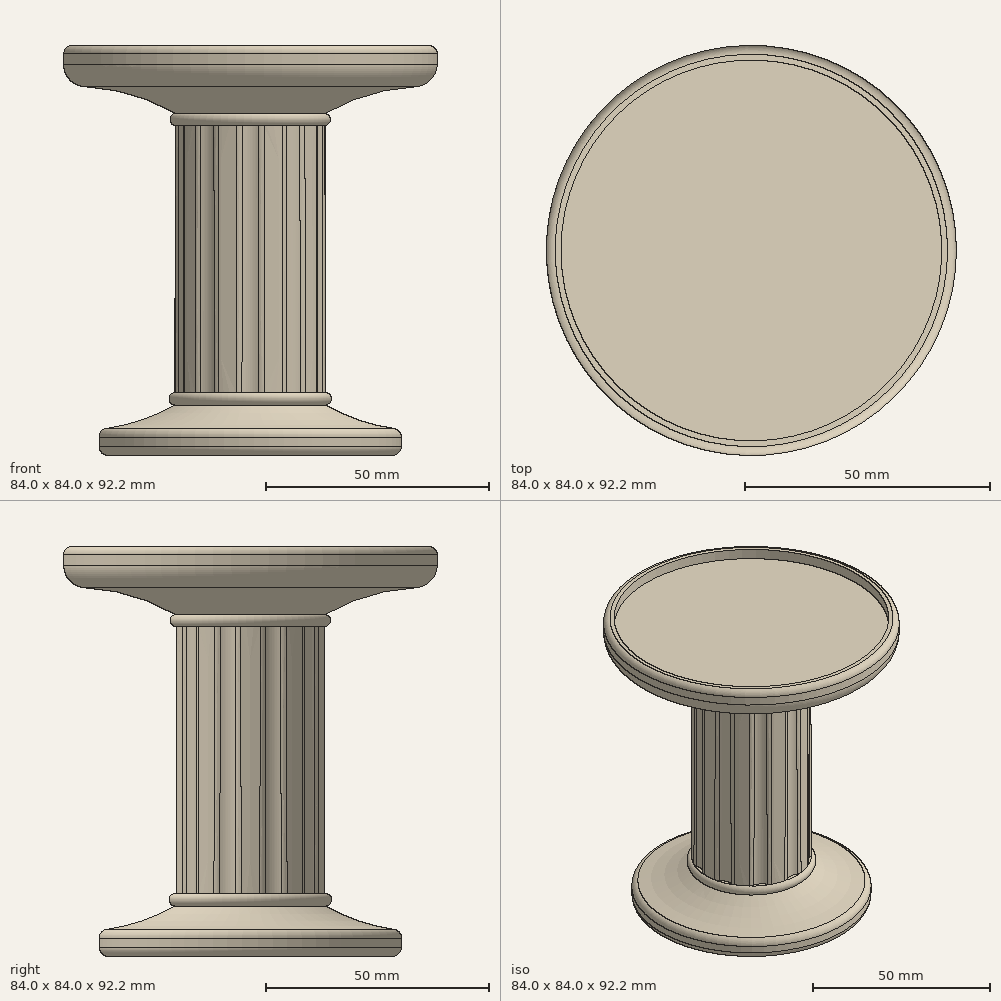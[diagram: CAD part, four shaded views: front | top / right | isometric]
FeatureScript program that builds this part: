
annotation { "Feature Type Name" : "Feature", "Feature Type Description" : "" }
export const myFeature = defineFeature(function(context is Context, id is Id, definition is map)
    precondition{}
    {
        {
            var Q0;
            Q0=qCreatedBy(makeId("Front.planeOp"),FACE);
            var sketch = newSketch(context, id + "F0", { "sketchPlane" : qUnion([Q0])});
            skLineSegment(sketch, "E0", {"start": v(-42, 62.68) * mm, "end": v(-42, 68.97) * mm});
            skLineSegment(sketch, "E1", {"start": v(-39, 68.97) * mm, "end": v(0, 68.97) * mm});
            skLineSegment(sketch, "E2", {"start": v(-34, -16.13) * mm, "end": v(-34, -18.24) * mm});
            skLineSegment(sketch, "E3", {"start": v(-32, -20.24) * mm, "end": v(0, -20.24) * mm});
            skLineSegment(sketch, "E4.0", {"start": v(-17, -6.1) * mm, "end": v(-16.89, 53.9) * mm});
            skArc(sketch, "E5", {"start": v(-16.88, 56.66) * mm, "mid": v(-29, 61.51) * mm, "end": v(-42, 62.68) * mm});
            skArc(sketch, "E6", {"start": v(-16.88, 56.66) * mm, "mid": v(-18.04, 55.29) * mm, "end": v(-16.89, 53.9) * mm});
            skArc(sketch, "E7.MirrorCS", {"start": v(-17, -8.88) * mm, "mid": v(-18.29, -7.49) * mm, "end": v(-17, -6.1) * mm});
            skArc(sketch, "E8.MirrorCS", {"start": v(-17, -8.88) * mm, "mid": v(-24.38, -12.26) * mm, "end": v(-32.27, -14.15) * mm});
            skLineSegment(sketch, "E9", {"start": v(-42, 68.97) * mm, "end": v(-42, 71.97) * mm});
            skLineSegment(sketch, "E10", {"start": v(-42, 71.97) * mm, "end": v(-39, 71.97) * mm});
            skLineSegment(sketch, "E11", {"start": v(-39, 71.97) * mm, "end": v(-39, 68.97) * mm});
            skPoint(sketch, "E12.visualSharp", {"position": v(-34, -20.24) * mm});
            skArc(sketch, "E12.filletArc", {"start": v(-34, -18.24) * mm, "mid": v(-33.41, -19.65) * mm, "end": v(-32, -20.24) * mm});
            skPoint(sketch, "E13.visualSharp", {"position": v(-34, -14.35) * mm});
            skArc(sketch, "E13.filletArc", {"start": v(-32.27, -14.15) * mm, "mid": v(-33.5, -14.81) * mm, "end": v(-34, -16.13) * mm});
            skLineSegment(sketch, "E14", {"start": v(0, -20.24) * mm, "end": v(0, 68.97) * mm});
            skSolve(sketch);
        }
        {
            var Q0;
            Q0=makeQuery(id+"F0.imprint","IMPRINT",FACE,{"disambiguationData":[TD([[makeQuery(id+"F0.imprint","IMPRINT",EDGE,{"derivedFrom":sQuery(id+"F0.wireOp",EDGE,"E0")}),-1.0]])]});
            var Q1;
            Q1=sQuery(id+"F0.wireOp",EDGE,"E14");
            revolve(context, id + "F1", {"entities" : qUnion([Q0]), "axis" : qUnion([Q1]), "revolveType" : RevolveType.FULL});
        }
        {
            var Q0;
            Q0=qCreatedBy(makeId("Top.planeOp"),FACE);
            cPlane(context, id + "F2", {"entities" : qUnion([Q0]), "cplaneType" : CPlaneType.OFFSET, "offset" : 6.1 * mm, "oppositeDirection" : true, "width" : 150 * mm, "height" : 150 * mm});
        }
        {
            var Q0;
            Q0=qCreatedBy(id+"F2.planeOp",FACE);
            var sketch = newSketch(context, id + "F3", { "sketchPlane" : qUnion([Q0])});
            skCircle(sketch, "E15", {"center": v(0, -20) * mm, "radius": 4 * mm});
            skCircle(sketch, "E16.1.0", {"center": v(11.76, -16.18) * mm, "radius": 4 * mm});
            skCircle(sketch, "E16.2.0", {"center": v(19.02, -6.18) * mm, "radius": 4 * mm});
            skCircle(sketch, "E16.3.0", {"center": v(19.02, 6.18) * mm, "radius": 4 * mm});
            skCircle(sketch, "E16.4.0", {"center": v(11.76, 16.18) * mm, "radius": 4 * mm});
            skCircle(sketch, "E16.5.0", {"center": v(0, 20) * mm, "radius": 4 * mm});
            skCircle(sketch, "E16.6.0", {"center": v(-11.76, 16.18) * mm, "radius": 4 * mm});
            skCircle(sketch, "E16.7.0", {"center": v(-19.02, 6.18) * mm, "radius": 4 * mm});
            skCircle(sketch, "E16.8.0", {"center": v(-19.02, -6.18) * mm, "radius": 4 * mm});
            skCircle(sketch, "E16.9.0", {"center": v(-11.76, -16.18) * mm, "radius": 4 * mm});
            skPoint(sketch, "E16.center", {"position": v(0, 0) * mm});
            skSolve(sketch);
        }
        {
            var Q0;
            Q0 = qSketchRegion(id + "F3", true);
            extrude(context, id + "F4", {"entities" : qUnion([Q0]), "operationType" : NewBodyOperationType.REMOVE, "depth" : 60 * mm});
        }
        {
            var Q0;
            Q0=makeQuery(id+"F4.boolean.opBoolean","INTERSECT",EDGE,{"disambiguationData":[OD(1.0)],"derivedFrom":[makeQuery(id+"F1.opRevolve","SWEPT_FACE",FACE,{"disambiguationData":[OSD([sQuery(id+"F0.wireOp",EDGE,"E4.0")])]}),makeQuery(id+"F4.opExtrude","SWEPT_FACE",FACE,{"disambiguationData":[OSD([sQuery(id+"F3.wireOp",EDGE,"E16.9.0")])]})]});
            var Q1;
            Q1=makeQuery(id+"F4.boolean.opBoolean","INTERSECT",EDGE,{"disambiguationData":[OD(0.0)],"derivedFrom":[makeQuery(id+"F1.opRevolve","SWEPT_FACE",FACE,{"disambiguationData":[OSD([sQuery(id+"F0.wireOp",EDGE,"E4.0")])]}),makeQuery(id+"F4.opExtrude","SWEPT_FACE",FACE,{"disambiguationData":[OSD([sQuery(id+"F3.wireOp",EDGE,"E15")])]})]});
            var Q2;
            Q2=makeQuery(id+"F4.boolean.opBoolean","INTERSECT",EDGE,{"disambiguationData":[OD(1.0)],"derivedFrom":[makeQuery(id+"F1.opRevolve","SWEPT_FACE",FACE,{"disambiguationData":[OSD([sQuery(id+"F0.wireOp",EDGE,"E4.0")])]}),makeQuery(id+"F4.opExtrude","SWEPT_FACE",FACE,{"disambiguationData":[OSD([sQuery(id+"F3.wireOp",EDGE,"E15")])]})]});
            var Q3;
            Q3=makeQuery(id+"F4.boolean.opBoolean","INTERSECT",EDGE,{"disambiguationData":[OD(0.0)],"derivedFrom":[makeQuery(id+"F1.opRevolve","SWEPT_FACE",FACE,{"disambiguationData":[OSD([sQuery(id+"F0.wireOp",EDGE,"E4.0")])]}),makeQuery(id+"F4.opExtrude","SWEPT_FACE",FACE,{"disambiguationData":[OSD([sQuery(id+"F3.wireOp",EDGE,"E16.9.0")])]})]});
            var Q4;
            Q4=makeQuery(id+"F4.boolean.opBoolean","INTERSECT",EDGE,{"disambiguationData":[OD(0.0)],"derivedFrom":[makeQuery(id+"F1.opRevolve","SWEPT_FACE",FACE,{"disambiguationData":[OSD([sQuery(id+"F0.wireOp",EDGE,"E4.0")])]}),makeQuery(id+"F4.opExtrude","SWEPT_FACE",FACE,{"disambiguationData":[OSD([sQuery(id+"F3.wireOp",EDGE,"E16.8.0")])]})]});
            var Q5;
            Q5=makeQuery(id+"F4.boolean.opBoolean","INTERSECT",EDGE,{"disambiguationData":[OD(1.0)],"derivedFrom":[makeQuery(id+"F1.opRevolve","SWEPT_FACE",FACE,{"disambiguationData":[OSD([sQuery(id+"F0.wireOp",EDGE,"E4.0")])]}),makeQuery(id+"F4.opExtrude","SWEPT_FACE",FACE,{"disambiguationData":[OSD([sQuery(id+"F3.wireOp",EDGE,"E16.8.0")])]})]});
            var Q6;
            Q6=makeQuery(id+"F4.boolean.opBoolean","INTERSECT",EDGE,{"disambiguationData":[OD(0.0)],"derivedFrom":[makeQuery(id+"F1.opRevolve","SWEPT_FACE",FACE,{"disambiguationData":[OSD([sQuery(id+"F0.wireOp",EDGE,"E4.0")])]}),makeQuery(id+"F4.opExtrude","SWEPT_FACE",FACE,{"disambiguationData":[OSD([sQuery(id+"F3.wireOp",EDGE,"E16.7.0")])]})]});
            var Q7;
            Q7=makeQuery(id+"F4.boolean.opBoolean","INTERSECT",EDGE,{"disambiguationData":[OD(1.0)],"derivedFrom":[makeQuery(id+"F1.opRevolve","SWEPT_FACE",FACE,{"disambiguationData":[OSD([sQuery(id+"F0.wireOp",EDGE,"E4.0")])]}),makeQuery(id+"F4.opExtrude","SWEPT_FACE",FACE,{"disambiguationData":[OSD([sQuery(id+"F3.wireOp",EDGE,"E16.7.0")])]})]});
            var Q8;
            Q8=makeQuery(id+"F4.boolean.opBoolean","INTERSECT",EDGE,{"disambiguationData":[OD(0.0)],"derivedFrom":[makeQuery(id+"F1.opRevolve","SWEPT_FACE",FACE,{"disambiguationData":[OSD([sQuery(id+"F0.wireOp",EDGE,"E4.0")])]}),makeQuery(id+"F4.opExtrude","SWEPT_FACE",FACE,{"disambiguationData":[OSD([sQuery(id+"F3.wireOp",EDGE,"E16.6.0")])]})]});
            var Q9;
            Q9=makeQuery(id+"F4.boolean.opBoolean","INTERSECT",EDGE,{"disambiguationData":[OD(1.0)],"derivedFrom":[makeQuery(id+"F1.opRevolve","SWEPT_FACE",FACE,{"disambiguationData":[OSD([sQuery(id+"F0.wireOp",EDGE,"E4.0")])]}),makeQuery(id+"F4.opExtrude","SWEPT_FACE",FACE,{"disambiguationData":[OSD([sQuery(id+"F3.wireOp",EDGE,"E16.6.0")])]})]});
            var Q10;
            Q10=makeQuery(id+"F4.boolean.opBoolean","INTERSECT",EDGE,{"disambiguationData":[OD(0.0)],"derivedFrom":[makeQuery(id+"F1.opRevolve","SWEPT_FACE",FACE,{"disambiguationData":[OSD([sQuery(id+"F0.wireOp",EDGE,"E4.0")])]}),makeQuery(id+"F4.opExtrude","SWEPT_FACE",FACE,{"disambiguationData":[OSD([sQuery(id+"F3.wireOp",EDGE,"E16.5.0")])]})]});
            var Q11;
            Q11=makeQuery(id+"F4.boolean.opBoolean","INTERSECT",EDGE,{"disambiguationData":[OD(1.0)],"derivedFrom":[makeQuery(id+"F1.opRevolve","SWEPT_FACE",FACE,{"disambiguationData":[OSD([sQuery(id+"F0.wireOp",EDGE,"E4.0")])]}),makeQuery(id+"F4.opExtrude","SWEPT_FACE",FACE,{"disambiguationData":[OSD([sQuery(id+"F3.wireOp",EDGE,"E16.5.0")])]})]});
            var Q12;
            Q12=makeQuery(id+"F4.boolean.opBoolean","INTERSECT",EDGE,{"disambiguationData":[OD(0.0)],"derivedFrom":[makeQuery(id+"F1.opRevolve","SWEPT_FACE",FACE,{"disambiguationData":[OSD([sQuery(id+"F0.wireOp",EDGE,"E4.0")])]}),makeQuery(id+"F4.opExtrude","SWEPT_FACE",FACE,{"disambiguationData":[OSD([sQuery(id+"F3.wireOp",EDGE,"E16.4.0")])]})]});
            var Q13;
            Q13=makeQuery(id+"F4.boolean.opBoolean","INTERSECT",EDGE,{"disambiguationData":[OD(1.0)],"derivedFrom":[makeQuery(id+"F1.opRevolve","SWEPT_FACE",FACE,{"disambiguationData":[OSD([sQuery(id+"F0.wireOp",EDGE,"E4.0")])]}),makeQuery(id+"F4.opExtrude","SWEPT_FACE",FACE,{"disambiguationData":[OSD([sQuery(id+"F3.wireOp",EDGE,"E16.4.0")])]})]});
            var Q14;
            Q14=makeQuery(id+"F4.boolean.opBoolean","INTERSECT",EDGE,{"disambiguationData":[OD(1.0)],"derivedFrom":[makeQuery(id+"F1.opRevolve","SWEPT_FACE",FACE,{"disambiguationData":[OSD([sQuery(id+"F0.wireOp",EDGE,"E4.0")])]}),makeQuery(id+"F4.opExtrude","SWEPT_FACE",FACE,{"disambiguationData":[OSD([sQuery(id+"F3.wireOp",EDGE,"E16.3.0")])]})]});
            var Q15;
            Q15=makeQuery(id+"F4.boolean.opBoolean","INTERSECT",EDGE,{"disambiguationData":[OD(0.0)],"derivedFrom":[makeQuery(id+"F1.opRevolve","SWEPT_FACE",FACE,{"disambiguationData":[OSD([sQuery(id+"F0.wireOp",EDGE,"E4.0")])]}),makeQuery(id+"F4.opExtrude","SWEPT_FACE",FACE,{"disambiguationData":[OSD([sQuery(id+"F3.wireOp",EDGE,"E16.3.0")])]})]});
            var Q16;
            Q16=makeQuery(id+"F4.boolean.opBoolean","INTERSECT",EDGE,{"disambiguationData":[OD(1.0)],"derivedFrom":[makeQuery(id+"F1.opRevolve","SWEPT_FACE",FACE,{"disambiguationData":[OSD([sQuery(id+"F0.wireOp",EDGE,"E4.0")])]}),makeQuery(id+"F4.opExtrude","SWEPT_FACE",FACE,{"disambiguationData":[OSD([sQuery(id+"F3.wireOp",EDGE,"E16.2.0")])]})]});
            var Q17;
            Q17=makeQuery(id+"F4.boolean.opBoolean","INTERSECT",EDGE,{"disambiguationData":[OD(0.0)],"derivedFrom":[makeQuery(id+"F1.opRevolve","SWEPT_FACE",FACE,{"disambiguationData":[OSD([sQuery(id+"F0.wireOp",EDGE,"E4.0")])]}),makeQuery(id+"F4.opExtrude","SWEPT_FACE",FACE,{"disambiguationData":[OSD([sQuery(id+"F3.wireOp",EDGE,"E16.2.0")])]})]});
            var Q18;
            Q18=makeQuery(id+"F4.boolean.opBoolean","INTERSECT",EDGE,{"disambiguationData":[OD(1.0)],"derivedFrom":[makeQuery(id+"F1.opRevolve","SWEPT_FACE",FACE,{"disambiguationData":[OSD([sQuery(id+"F0.wireOp",EDGE,"E4.0")])]}),makeQuery(id+"F4.opExtrude","SWEPT_FACE",FACE,{"disambiguationData":[OSD([sQuery(id+"F3.wireOp",EDGE,"E16.1.0")])]})]});
            var Q19;
            Q19=makeQuery(id+"F4.boolean.opBoolean","INTERSECT",EDGE,{"disambiguationData":[OD(0.0)],"derivedFrom":[makeQuery(id+"F1.opRevolve","SWEPT_FACE",FACE,{"disambiguationData":[OSD([sQuery(id+"F0.wireOp",EDGE,"E4.0")])]}),makeQuery(id+"F4.opExtrude","SWEPT_FACE",FACE,{"disambiguationData":[OSD([sQuery(id+"F3.wireOp",EDGE,"E16.1.0")])]})]});
            fillet(context, id + "F5", {"entities" : qUnion([Q0, Q1, Q2, Q3, Q4, Q5, Q6, Q7, Q8, Q9, Q10, Q11, Q12, Q13, Q14, Q15, Q16, Q17, Q18, Q19]), "radius" : 2 * mm, "tangentPropagation" : true, "allowEdgeOverflow" : false});
        }
        {
            var Q0;
            Q0=makeQuery(id+"F1.opRevolve","SWEPT_EDGE",EDGE,{"disambiguationData":[OSD([sQuery(id+"F0.wireOp",EDGE,"E0"),sQuery(id+"F0.wireOp",EDGE,"E5")])]});
            fillet(context, id + "F6", {"entities" : qUnion([Q0]), "radius" : 5 * mm, "tangentPropagation" : true, "allowEdgeOverflow" : false});
        }
        {
            var Q0;
            Q0=makeQuery(id+"F1.opRevolve","SWEPT_EDGE",EDGE,{"disambiguationData":[OSD([sQuery(id+"F0.wireOp",EDGE,"E9"),sQuery(id+"F0.wireOp",EDGE,"E10")])]});
            fillet(context, id + "F7", {"entities" : qUnion([Q0]), "radius" : 1.81 * mm, "tangentPropagation" : true, "allowEdgeOverflow" : false});
        }
        {
            var Q0;
            Q0=makeQuery(id+"F1.opRevolve","SWEPT_FACE",FACE,{"disambiguationData":[OSD([sQuery(id+"F0.wireOp",EDGE,"E3")])]});
            var sketch = newSketch(context, id + "F8", { "sketchPlane" : qUnion([Q0])});
            skText(sketch, "E17", { "text": "R3D", "fontName": "OpenSans-BoldItalic.ttf"});
            const initialGuessF8  = {"E17": [-0.02706, -0.00928, 1, 0, 0.0214]};
            skSetInitialGuess(sketch, initialGuessF8);
            skSolve(sketch);
        }
        {
            var Q0;
            Q0 = qSketchRegion(id + "F8", true);
            extrude(context, id + "F9", {"entities" : qUnion([Q0]), "operationType" : NewBodyOperationType.REMOVE, "oppositeDirection" : true, "depth" : 1 * mm});
        }
    });
